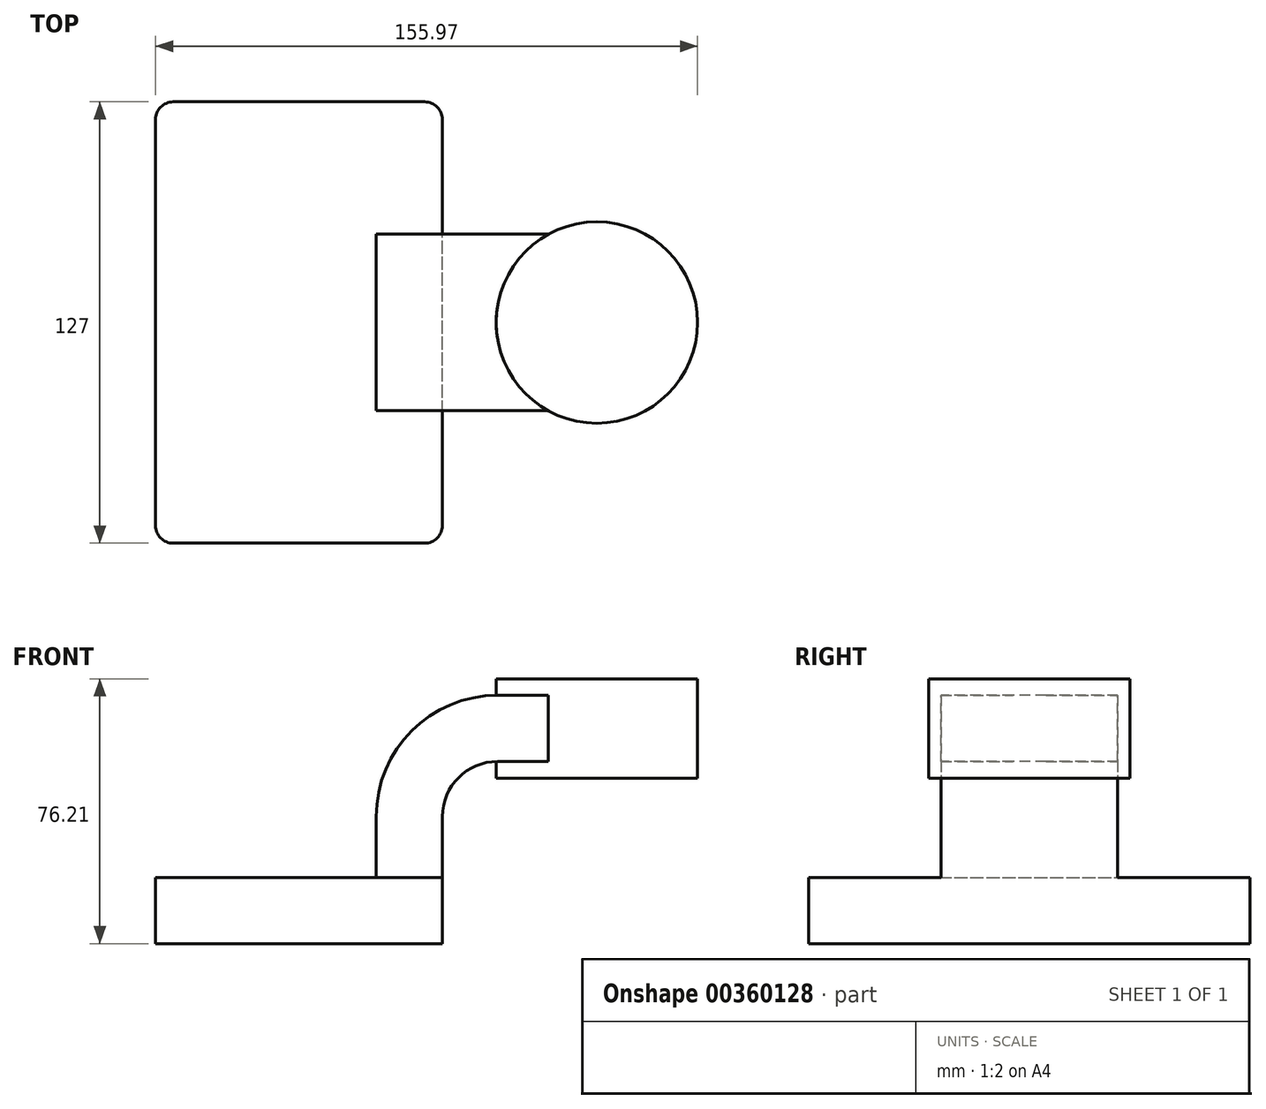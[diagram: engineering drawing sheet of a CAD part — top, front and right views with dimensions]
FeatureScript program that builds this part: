
annotation { "Feature Type Name" : "Feature", "Feature Type Description" : "" }
export const myFeature = defineFeature(function(context is Context, id is Id, definition is map)
    precondition{}
    {
        {
            var Q0;
            Q0=qCreatedBy(makeId("Front.planeOp"),FACE);
            var sketch = newSketch(context, id + "F0", { "sketchPlane" : qUnion([Q0])});
            skLineSegment(sketch, "E0.bottom", {"start": v(-41.28, -9.53) * mm, "end": v(41.28, -9.53) * mm});
            skLineSegment(sketch, "E0.top", {"start": v(-41.28, 9.53) * mm, "end": v(41.28, 9.53) * mm});
            skLineSegment(sketch, "E0.left", {"start": v(-41.28, -9.53) * mm, "end": v(-41.28, 9.53) * mm});
            skLineSegment(sketch, "E0.right", {"start": v(41.28, -9.53) * mm, "end": v(41.28, 9.53) * mm});
            skPoint(sketch, "E0.middle", {"position": v(0, 0) * mm});
            skLineSegment(sketch, "E1.bottom", {"start": v(63.9, 38.1) * mm, "end": v(114.7, 38.1) * mm});
            skLineSegment(sketch, "E1.top", {"start": v(63.9, 66.67) * mm, "end": v(114.7, 66.67) * mm});
            skLineSegment(sketch, "E1.left", {"start": v(63.9, 38.1) * mm, "end": v(63.9, 66.67) * mm});
            skLineSegment(sketch, "E1.right", {"start": v(114.7, 38.1) * mm, "end": v(114.7, 66.67) * mm});
            skPoint(sketch, "E1.middle", {"position": v(89.3, 52.39) * mm});
            skLineSegment(sketch, "E2", {"start": v(41.28, 9.52) * mm, "end": v(41.28, 27) * mm});
            skArc(sketch, "E3", {"start": v(41.27, 27) * mm, "mid": v(45.92, 38.23) * mm, "end": v(57.15, 42.88) * mm});
            skLineSegment(sketch, "E4", {"start": v(57.15, 42.88) * mm, "end": v(85.72, 42.88) * mm});
            skLineSegment(sketch, "E5.0", {"start": v(57.15, 61.93) * mm, "end": v(85.72, 61.93) * mm});
            skArc(sketch, "E5.1", {"start": v(22.22, 27) * mm, "mid": v(32.45, 51.7) * mm, "end": v(57.15, 61.93) * mm});
            skLineSegment(sketch, "E5.2", {"start": v(22.22, 9.52) * mm, "end": v(22.22, 27) * mm});
            skLineSegment(sketch, "E6", {"start": v(85.72, 66.67) * mm, "end": v(85.72, 38.1) * mm});
            skPoint(sketch, "E6.startSnap0", {"position": v(89.3, 66.67) * mm});
            skFitSpline(sketch, "E7", {"points": [v(-41.28, 9.52) * mm, v(57.15, 61.93) * mm], "startDerivative": vector(60.88, 118.38) * mm, "endDerivative": vector(153.37, -1.35) * mm});
            skSolve(sketch);
        }
        {
            var Q0;
            Q0=makeQuery(id+"F0.imprint","IMPRINT",FACE,{"disambiguationData":[TD([[makeQuery(id+"F0.imprint","IMPRINT",EDGE,{"derivedFrom":sQuery(id+"F0.wireOp",EDGE,"E0.bottom")}),1.0]])]});
            extrude(context, id + "F1", {"entities" : qUnion([Q0]), "endBound" : BoundingType.SYMMETRIC, "depth" : 127 * mm});
        }
        {
            var Q0;
            {var subQ1=sQuery(id+"F0.wireOp",EDGE,"E2");Q0=makeQuery(id+"F0.imprint","IMPRINT",FACE,{"disambiguationData":[TD([[makeQuery(id+"F0.imprint","IMPRINT",EDGE,{"derivedFrom":subQ1}),1.0]])]});}
            var Q1;
            {var subQ0=sQuery(id+"F0.wireOp",EDGE,"E4");var subQ1=sQuery(id+"F0.wireOp",EDGE,"E1.left");var subQ2=makeQuery(id+"F0.imprint","INTERSECT",VERTEX,{"derivedFrom":[subQ1,subQ0]});Q1=makeQuery(id+"F0.imprint","IMPRINT",FACE,{"disambiguationData":[TD([[makeQuery(id+"F0.imprint","IMPRINT",EDGE,{"disambiguationData":[TD([[subQ2,-1.0]])],"derivedFrom":subQ1}),-1.0]])]});}
            extrude(context, id + "F2", {"entities" : qUnion([Q0, Q1]), "operationType" : NewBodyOperationType.ADD, "endBound" : BoundingType.SYMMETRIC, "depth" : 50.8 * mm});
        }
        {
            var Q0;
            Q0=makeQuery(id+"F0.imprint","IMPRINT",FACE,{"disambiguationData":[TD([[makeQuery(id+"F0.imprint","IMPRINT",EDGE,{"derivedFrom":sQuery(id+"F0.wireOp",EDGE,"E5.1")}),1.0]])]});
            extrude(context, id + "F3", {"entities" : qUnion([Q0]), "operationType" : NewBodyOperationType.ADD, "endBound" : BoundingType.SYMMETRIC, "depth" : 15.88 * mm});
        }
        {
            var Q0;
            {var subQ0=sQuery(id+"F0.wireOp",EDGE,"E1.right");Q0=makeQuery(id+"F0.imprint","IMPRINT",FACE,{"disambiguationData":[TD([[makeQuery(id+"F0.imprint","IMPRINT",EDGE,{"derivedFrom":subQ0}),1.0]])]});}
            var Q1;
            Q1=sQuery(id+"F0.wireOp",EDGE,"E6");
            revolve(context, id + "F4", {"operationType" : NewBodyOperationType.ADD, "entities" : qUnion([Q0]), "axis" : qUnion([Q1]), "revolveType" : RevolveType.FULL});
        }
        {
            var Q0;
            Q0=makeQuery(id+"F1.opExtrude","CAP_EDGE",EDGE,{"disambiguationData":[OSD([sQuery(id+"F0.wireOp",EDGE,"E0.right")])],"isStart":false});
            var Q1;
            Q1=makeQuery(id+"F1.opExtrude","CAP_EDGE",EDGE,{"disambiguationData":[OSD([sQuery(id+"F0.wireOp",EDGE,"E0.left")])],"isStart":false});
            var Q2;
            Q2=makeQuery(id+"F1.opExtrude","CAP_EDGE",EDGE,{"disambiguationData":[OSD([sQuery(id+"F0.wireOp",EDGE,"E0.right")])],"isStart":true});
            var Q3;
            Q3=makeQuery(id+"F1.opExtrude","CAP_EDGE",EDGE,{"disambiguationData":[OSD([sQuery(id+"F0.wireOp",EDGE,"E0.left")])],"isStart":true});
            fillet(context, id + "F5", {"entities" : qUnion([Q0, Q1, Q2, Q3]), "radius" : 5.08 * mm, "tangentPropagation" : true, "allowEdgeOverflow" : false});
        }
    });
